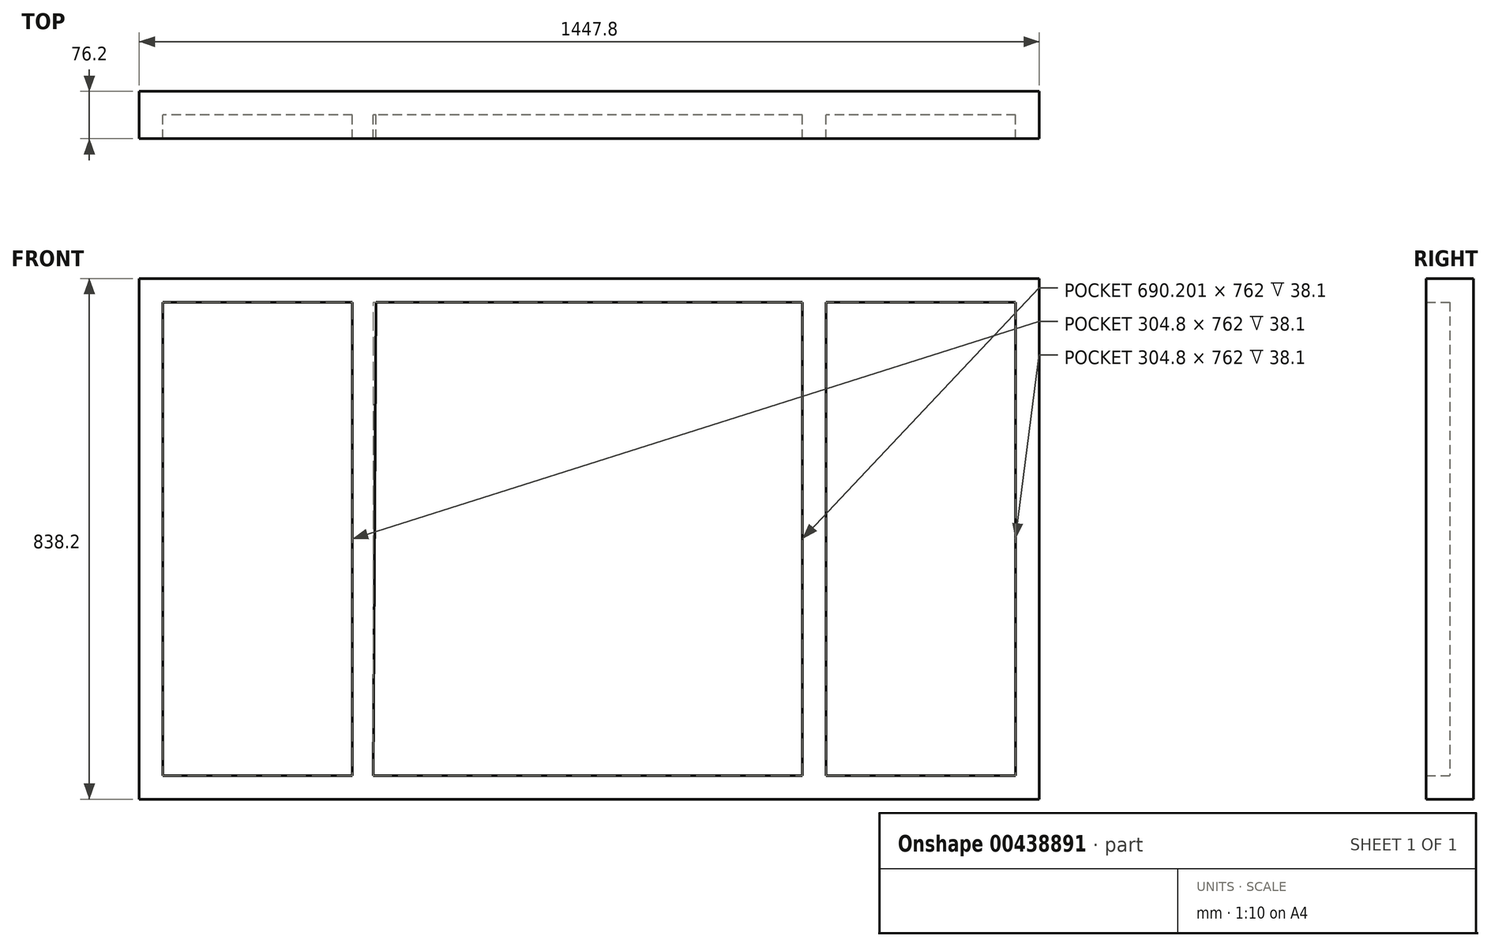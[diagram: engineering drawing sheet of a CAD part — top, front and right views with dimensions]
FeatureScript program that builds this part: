
annotation { "Feature Type Name" : "Feature", "Feature Type Description" : "" }
export const myFeature = defineFeature(function(context is Context, id is Id, definition is map)
    precondition{}
    {
        {
            var Q0;
            Q0=qCreatedBy(makeId("Front.planeOp"),FACE);
            var sketch = newSketch(context, id + "F0", { "sketchPlane" : qUnion([Q0])});
            skLineSegment(sketch, "E0.bottom", {"start": v(0, 0) * mm, "end": v(-1447.8, 0) * mm});
            skLineSegment(sketch, "E0.top", {"start": v(0, -838.2) * mm, "end": v(-1447.8, -838.2) * mm});
            skLineSegment(sketch, "E0.left", {"start": v(0, 0) * mm, "end": v(0, -838.2) * mm});
            skLineSegment(sketch, "E0.right", {"start": v(-1447.8, 0) * mm, "end": v(-1447.8, -838.2) * mm});
            skLineSegment(sketch, "E1.bottom", {"start": v(-38.1, -38.1) * mm, "end": v(-1409.7, -38.1) * mm});
            skLineSegment(sketch, "E1.top", {"start": v(-38.1, -800.1) * mm, "end": v(-1409.7, -800.1) * mm});
            skLineSegment(sketch, "E1.left", {"start": v(-38.1, -38.1) * mm, "end": v(-38.1, -800.1) * mm});
            skLineSegment(sketch, "E1.right", {"start": v(-1409.7, -38.1) * mm, "end": v(-1409.7, -800.1) * mm});
            skLineSegment(sketch, "E2", {"start": v(-38.1, -228.6) * mm, "end": v(-1409.7, -228.6) * mm});
            skLineSegment(sketch, "E3", {"start": v(-38.1, -427.02) * mm, "end": v(-1409.7, -419.1) * mm});
            skLineSegment(sketch, "E4", {"start": v(-38.1, -609.6) * mm, "end": v(-1409.7, -601.68) * mm});
            skLineSegment(sketch, "E5", {"start": v(-1104.9, -38.1) * mm, "end": v(-1104.9, -800.1) * mm});
            skLineSegment(sketch, "E6", {"start": v(-1071.2, -800.1) * mm, "end": v(-1066.8, -38.1) * mm});
            skLineSegment(sketch, "E7", {"start": v(-342.9, -38.1) * mm, "end": v(-342.9, -800.1) * mm});
            skLineSegment(sketch, "E8", {"start": v(-381, -800.1) * mm, "end": v(-381, -38.1) * mm});
            skSolve(sketch);
        }
        {
            var Q0;
            {var subQ0=sQuery(id+"F0.wireOp",EDGE,"E1.bottom");Q0=makeQuery(id+"F0.imprint","IMPRINT",FACE,{"disambiguationData":[TD([[makeQuery(id+"F0.imprint","IMPRINT",EDGE,{"derivedFrom":subQ0}),1.0]])]});}
            extrude(context, id + "F1", {"entities" : qUnion([Q0]), "depth" : 38.1 * mm});
        }
        {
            var Q0;
            {var subQ0=sQuery(id+"F0.wireOp",EDGE,"E2");Q0=makeQuery(id+"F0.imprint","IMPRINT",FACE,{"disambiguationData":[TD([[makeQuery(id+"F0.imprint","IMPRINT",EDGE,{"derivedFrom":subQ0}),1.0]])]});}
            extrude(context, id + "F2", {"entities" : qUnion([Q0]), "operationType" : NewBodyOperationType.ADD, "depth" : 38.1 * mm});
        }
        {
            var Q0;
            {var subQ0=sQuery(id+"F0.wireOp",EDGE,"E3");Q0=makeQuery(id+"F0.imprint","IMPRINT",FACE,{"disambiguationData":[TD([[makeQuery(id+"F0.imprint","IMPRINT",EDGE,{"derivedFrom":subQ0}),1.0]])]});}
            extrude(context, id + "F3", {"entities" : qUnion([Q0]), "operationType" : NewBodyOperationType.ADD, "depth" : 38.1 * mm});
        }
        {
            var Q0;
            {var subQ0=sQuery(id+"F0.wireOp",EDGE,"E1.top");Q0=makeQuery(id+"F0.imprint","IMPRINT",FACE,{"disambiguationData":[TD([[makeQuery(id+"F0.imprint","IMPRINT",EDGE,{"derivedFrom":subQ0}),-1.0]])]});}
            extrude(context, id + "F4", {"entities" : qUnion([Q0]), "operationType" : NewBodyOperationType.ADD, "depth" : 38.1 * mm});
        }
        {
            var Q0;
            Q0=makeQuery(id+"F0.imprint","IMPRINT",FACE,{"disambiguationData":[TD([[makeQuery(id+"F0.imprint","IMPRINT",EDGE,{"derivedFrom":sQuery(id+"F0.wireOp",EDGE,"E0.bottom")}),1.0]])]});
            extrude(context, id + "F5", {"entities" : qUnion([Q0]), "operationType" : NewBodyOperationType.ADD, "depth" : 76.2 * mm});
        }
        {
            var Q0;
            {var subQ0=sQuery(id+"F0.wireOp",EDGE,"E5");var subQ1=sQuery(id+"F0.wireOp",EDGE,"E1.bottom");var subQ2=makeQuery(id+"F0.imprint","INTERSECT",VERTEX,{"derivedFrom":[subQ1,subQ0]});Q0=makeQuery(id+"F0.imprint","IMPRINT",FACE,{"disambiguationData":[TD([[makeQuery(id+"F0.imprint","IMPRINT",EDGE,{"disambiguationData":[TD([[subQ2,1.0]])],"derivedFrom":subQ1}),1.0]])]});}
            var Q1;
            {var subQ0=sQuery(id+"F0.wireOp",EDGE,"E6");var subQ1=sQuery(id+"F0.wireOp",EDGE,"E2");var subQ2=makeQuery(id+"F0.imprint","INTERSECT",VERTEX,{"derivedFrom":[subQ1,subQ0]});Q1=makeQuery(id+"F0.imprint","IMPRINT",FACE,{"disambiguationData":[TD([[makeQuery(id+"F0.imprint","IMPRINT",EDGE,{"disambiguationData":[TD([[subQ2,-1.0]])],"derivedFrom":subQ1}),1.0]])]});}
            var Q2;
            {var subQ0=sQuery(id+"F0.wireOp",EDGE,"E6");var subQ1=sQuery(id+"F0.wireOp",EDGE,"E3");var subQ2=makeQuery(id+"F0.imprint","INTERSECT",VERTEX,{"derivedFrom":[subQ1,subQ0]});Q2=makeQuery(id+"F0.imprint","IMPRINT",FACE,{"disambiguationData":[TD([[makeQuery(id+"F0.imprint","IMPRINT",EDGE,{"disambiguationData":[TD([[subQ2,-1.0]])],"derivedFrom":subQ1}),1.0]])]});}
            var Q3;
            {var subQ0=sQuery(id+"F0.wireOp",EDGE,"E5");var subQ1=sQuery(id+"F0.wireOp",EDGE,"E1.top");var subQ2=makeQuery(id+"F0.imprint","INTERSECT",VERTEX,{"derivedFrom":[subQ1,subQ0]});Q3=makeQuery(id+"F0.imprint","IMPRINT",FACE,{"disambiguationData":[TD([[makeQuery(id+"F0.imprint","IMPRINT",EDGE,{"disambiguationData":[TD([[subQ2,1.0]])],"derivedFrom":subQ1}),-1.0]])]});}
            extrude(context, id + "F6", {"entities" : qUnion([Q0, Q1, Q2, Q3]), "operationType" : NewBodyOperationType.ADD, "depth" : 76.2 * mm});
        }
        {
            var Q0;
            {var subQ0=sQuery(id+"F0.wireOp",EDGE,"E7");var subQ1=sQuery(id+"F0.wireOp",EDGE,"E1.bottom");var subQ2=makeQuery(id+"F0.imprint","INTERSECT",VERTEX,{"derivedFrom":[subQ1,subQ0]});Q0=makeQuery(id+"F0.imprint","IMPRINT",FACE,{"disambiguationData":[TD([[makeQuery(id+"F0.imprint","IMPRINT",EDGE,{"disambiguationData":[TD([[subQ2,-1.0]])],"derivedFrom":subQ1}),1.0]])]});}
            var Q1;
            {var subQ0=sQuery(id+"F0.wireOp",EDGE,"E7");var subQ1=sQuery(id+"F0.wireOp",EDGE,"E2");var subQ2=makeQuery(id+"F0.imprint","INTERSECT",VERTEX,{"derivedFrom":[subQ1,subQ0]});Q1=makeQuery(id+"F0.imprint","IMPRINT",FACE,{"disambiguationData":[TD([[makeQuery(id+"F0.imprint","IMPRINT",EDGE,{"disambiguationData":[TD([[subQ2,-1.0]])],"derivedFrom":subQ1}),1.0]])]});}
            var Q2;
            {var subQ0=sQuery(id+"F0.wireOp",EDGE,"E7");var subQ1=sQuery(id+"F0.wireOp",EDGE,"E3");var subQ2=makeQuery(id+"F0.imprint","INTERSECT",VERTEX,{"derivedFrom":[subQ1,subQ0]});Q2=makeQuery(id+"F0.imprint","IMPRINT",FACE,{"disambiguationData":[TD([[makeQuery(id+"F0.imprint","IMPRINT",EDGE,{"disambiguationData":[TD([[subQ2,-1.0]])],"derivedFrom":subQ1}),1.0]])]});}
            var Q3;
            {var subQ0=sQuery(id+"F0.wireOp",EDGE,"E7");var subQ1=sQuery(id+"F0.wireOp",EDGE,"E1.top");var subQ2=makeQuery(id+"F0.imprint","INTERSECT",VERTEX,{"derivedFrom":[subQ1,subQ0]});Q3=makeQuery(id+"F0.imprint","IMPRINT",FACE,{"disambiguationData":[TD([[makeQuery(id+"F0.imprint","IMPRINT",EDGE,{"disambiguationData":[TD([[subQ2,-1.0]])],"derivedFrom":subQ1}),-1.0]])]});}
            extrude(context, id + "F7", {"entities" : qUnion([Q0, Q1, Q2, Q3]), "operationType" : NewBodyOperationType.ADD, "depth" : 76.2 * mm});
        }
    });
